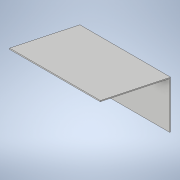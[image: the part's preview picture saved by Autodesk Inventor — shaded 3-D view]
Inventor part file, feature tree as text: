
AUTODESK INVENTOR PART (.ipt)
format: ipt  version: 2021 (Build 250183000, 183)  size: 97,280 bytes
history: native  units: in
note: dims shown in document units (in); Inventor stores cm internally (conversion verified against a paired STEP export)
features: extrude x1, sketch x1
ambient origin geometry x8: Origin, YZ Plane, XZ Plane, XY Plane, X Axis, Y Axis, Z Axis, Center Point
bodies: Solid1 (feature_tree)
feature tree (2):
  extrude  "Extrusion1"  Depth=0.125in
  sketch  "Sketch1"  dims[d0=6.25in d1=0.125in d2=9.5in d3=0.536in d4=0.125in d5=0.125in d6=12.0in d7=0.0in]
